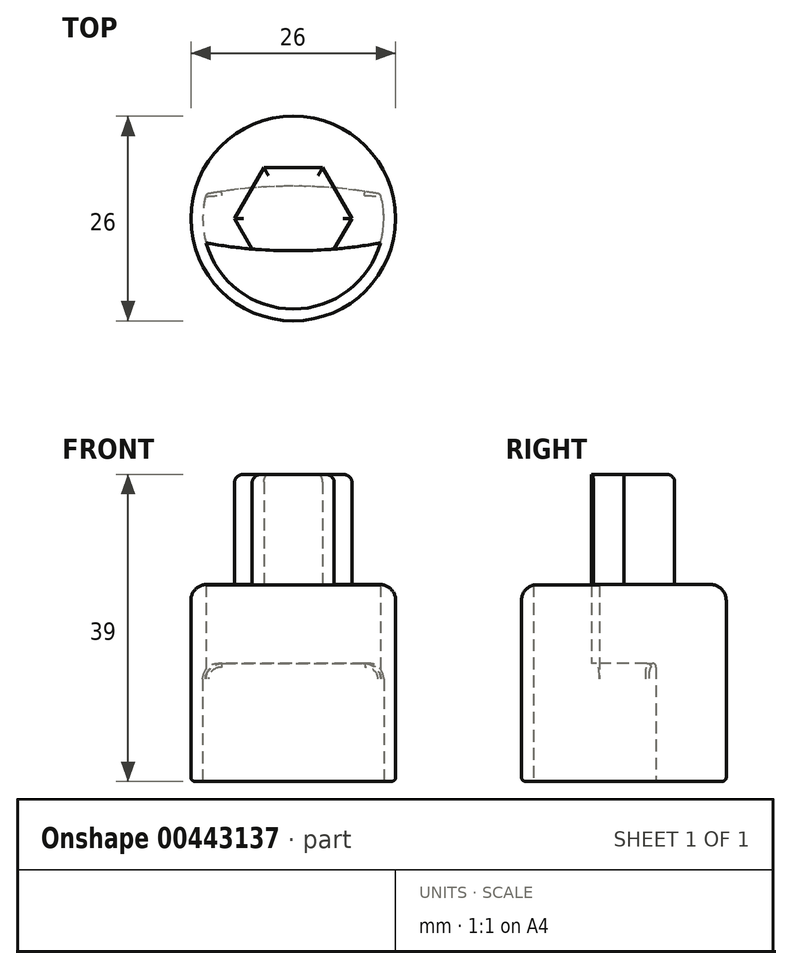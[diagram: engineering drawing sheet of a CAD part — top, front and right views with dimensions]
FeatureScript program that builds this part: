
annotation { "Feature Type Name" : "Feature", "Feature Type Description" : "" }
export const myFeature = defineFeature(function(context is Context, id is Id, definition is map)
    precondition{}
    {
        {
            var Q0;
            Q0=qCreatedBy(makeId("Top.planeOp"),FACE);
            var sketch = newSketch(context, id + "F0", { "sketchPlane" : qUnion([Q0])});
            skCircle(sketch, "E0", {"center": v(0, 0) * mm, "radius": 13 * mm});
            skCircle(sketch, "E1", {"center": v(0, 0) * mm, "radius": 11.5 * mm});
            skArc(sketch, "E2", {"start": v(11.07, 3.1) * mm, "mid": v(0, 4.1) * mm, "end": v(-11.07, 3.1) * mm});
            skLineSegment(sketch, "E3", {"start": v(-11.07, 3.1) * mm, "end": v(11.07, 3.1) * mm, "construction": true});
            skArc(sketch, "E4.MirrorCS", {"start": v(11.07, -3.1) * mm, "mid": v(0, -4.1) * mm, "end": v(-11.07, -3.1) * mm});
            skSolve(sketch);
        }
        {
            var Q0;
            Q0=makeQuery(id+"F0.imprint","IMPRINT",FACE,{"disambiguationData":[TD([[makeQuery(id+"F0.imprint","IMPRINT",EDGE,{"derivedFrom":sQuery(id+"F0.wireOp",EDGE,"E0")}),1.0]])]});
            var Q1;
            {var subQ0=sQuery(id+"F0.wireOp",EDGE,"E2");Q1=makeQuery(id+"F0.imprint","IMPRINT",FACE,{"disambiguationData":[TD([[makeQuery(id+"F0.imprint","IMPRINT",EDGE,{"derivedFrom":subQ0}),-1.0]])]});}
            var Q2;
            {var subQ0=sQuery(id+"F0.wireOp",EDGE,"E4.MirrorCS");Q2=makeQuery(id+"F0.imprint","IMPRINT",FACE,{"disambiguationData":[TD([[makeQuery(id+"F0.imprint","IMPRINT",EDGE,{"derivedFrom":subQ0}),1.0]])]});}
            var Q3;
            {var subQ0=sQuery(id+"F0.wireOp",EDGE,"E2");Q3=makeQuery(id+"F0.imprint","IMPRINT",FACE,{"disambiguationData":[TD([[makeQuery(id+"F0.imprint","IMPRINT",EDGE,{"derivedFrom":subQ0}),1.0]])]});}
            extrude(context, id + "F1", {"entities" : qUnion([Q0, Q1, Q2, Q3]), "depth" : 25 * mm});
        }
        {
            var Q0;
            {var subQ0=sQuery(id+"F0.wireOp",EDGE,"E2");Q0=makeQuery(id+"F0.imprint","IMPRINT",FACE,{"disambiguationData":[TD([[makeQuery(id+"F0.imprint","IMPRINT",EDGE,{"derivedFrom":subQ0}),1.0]])]});}
            extrude(context, id + "F2", {"entities" : qUnion([Q0]), "operationType" : NewBodyOperationType.REMOVE, "depth" : 15 * mm});
        }
        {
            var Q0;
            Q0=makeQuery(id+"F1.opExtrude","CAP_FACE",FACE,{"disambiguationData":[OSD([sQuery(id+"F0.wireOp",EDGE,"E0")])],"isStart":false});
            var sketch = newSketch(context, id + "F3", { "sketchPlane" : qUnion([Q0])});
            skCircle(sketch, "E5.cCircle", {"center": v(0, 0) * mm, "radius": 6.45 * mm, "construction": true});
            skLineSegment(sketch, "E5.0", {"start": v(-3.72, 6.45) * mm, "end": v(3.72, 6.45) * mm});
            skLineSegment(sketch, "E5.1", {"start": v(3.72, 6.45) * mm, "end": v(7.45, 0) * mm});
            skLineSegment(sketch, "E5.2", {"start": v(7.45, 0) * mm, "end": v(3.72, -6.45) * mm});
            skLineSegment(sketch, "E5.3", {"start": v(3.72, -6.45) * mm, "end": v(-3.72, -6.45) * mm});
            skLineSegment(sketch, "E5.4", {"start": v(-3.72, -6.45) * mm, "end": v(-7.45, 0) * mm});
            skLineSegment(sketch, "E5.5", {"start": v(-7.45, 0) * mm, "end": v(-3.72, 6.45) * mm});
            skPoint(sketch, "E5.0.midPoint", {"position": v(0, 6.45) * mm});
            skSolve(sketch);
        }
        {
            var Q0;
            Q0=makeQuery(id+"F3.imprint","IMPRINT",FACE,{"disambiguationData":[TD([[makeQuery(id+"F3.imprint","IMPRINT",EDGE,{"derivedFrom":sQuery(id+"F3.wireOp",EDGE,"E5.0")}),-1.0]])]});
            extrude(context, id + "F4", {"entities" : qUnion([Q0]), "operationType" : NewBodyOperationType.ADD, "depth" : 14 * mm});
        }
        {
            var Q0;
            Q0=makeQuery(id+"F4.opExtrude","CAP_EDGE",EDGE,{"disambiguationData":[OSD([sQuery(id+"F3.wireOp",EDGE,"E5.5")])],"isStart":true});
            var Q1;
            Q1=makeQuery(id+"F4.opExtrude","CAP_EDGE",EDGE,{"disambiguationData":[OSD([sQuery(id+"F3.wireOp",EDGE,"E5.4")])],"isStart":true});
            var Q2;
            Q2=makeQuery(id+"F4.opExtrude","CAP_EDGE",EDGE,{"disambiguationData":[OSD([sQuery(id+"F3.wireOp",EDGE,"E5.3")])],"isStart":true});
            var Q3;
            Q3=makeQuery(id+"F4.opExtrude","CAP_EDGE",EDGE,{"disambiguationData":[OSD([sQuery(id+"F3.wireOp",EDGE,"E5.2")])],"isStart":true});
            var Q4;
            Q4=makeQuery(id+"F4.opExtrude","CAP_EDGE",EDGE,{"disambiguationData":[OSD([sQuery(id+"F3.wireOp",EDGE,"E5.1")])],"isStart":true});
            var Q5;
            Q5=makeQuery(id+"F4.opExtrude","CAP_EDGE",EDGE,{"disambiguationData":[OSD([sQuery(id+"F3.wireOp",EDGE,"E5.0")])],"isStart":true});
            var Q6;
            Q6=makeQuery(id+"F4.opExtrude","CAP_EDGE",EDGE,{"disambiguationData":[OSD([sQuery(id+"F3.wireOp",EDGE,"E5.5")])],"isStart":false});
            var Q7;
            Q7=makeQuery(id+"F4.opExtrude","CAP_EDGE",EDGE,{"disambiguationData":[OSD([sQuery(id+"F3.wireOp",EDGE,"E5.0")])],"isStart":false});
            var Q8;
            Q8=makeQuery(id+"F4.opExtrude","CAP_EDGE",EDGE,{"disambiguationData":[OSD([sQuery(id+"F3.wireOp",EDGE,"E5.1")])],"isStart":false});
            var Q9;
            Q9=makeQuery(id+"F4.opExtrude","CAP_EDGE",EDGE,{"disambiguationData":[OSD([sQuery(id+"F3.wireOp",EDGE,"E5.4")])],"isStart":false});
            var Q10;
            Q10=makeQuery(id+"F4.opExtrude","CAP_EDGE",EDGE,{"disambiguationData":[OSD([sQuery(id+"F3.wireOp",EDGE,"E5.3")])],"isStart":false});
            var Q11;
            Q11=makeQuery(id+"F4.opExtrude","CAP_EDGE",EDGE,{"disambiguationData":[OSD([sQuery(id+"F3.wireOp",EDGE,"E5.2")])],"isStart":false});
            fillet(context, id + "F5", {"entities" : qUnion([Q0, Q1, Q2, Q3, Q4, Q5, Q6, Q7, Q8, Q9, Q10, Q11]), "radius" : 1 * mm, "tangentPropagation" : true, "allowEdgeOverflow" : false});
        }
        {
            var Q0;
            {var subQ0=sQuery(id+"F0.wireOp",EDGE,"E1");Q0=makeQuery(id+"F2.boolean.opBoolean","COPY",EDGE,{"derivedFrom":makeQuery(id+"F2.opExtrude","CAP_EDGE",EDGE,{"disambiguationData":[OSD([subQ0]),TDD([makeQuery(id+"F0.imprint","IMPRINT",EDGE,{"disambiguationData":[TD([[makeQuery(id+"F0.imprint","INTERSECT",VERTEX,{"disambiguationData":[OD(0.0)],"derivedFrom":[subQ0,sQuery(id+"F0.wireOp",EDGE,"E2")]}),1.0]])],"derivedFrom":subQ0})])],"isStart":false})});}
            var Q1;
            {var subQ0=sQuery(id+"F0.wireOp",EDGE,"E1");Q1=makeQuery(id+"F2.boolean.opBoolean","COPY",EDGE,{"derivedFrom":makeQuery(id+"F2.opExtrude","CAP_EDGE",EDGE,{"disambiguationData":[OSD([subQ0]),TDD([makeQuery(id+"F0.imprint","IMPRINT",EDGE,{"disambiguationData":[TD([[makeQuery(id+"F0.imprint","INTERSECT",VERTEX,{"disambiguationData":[OD(1.0)],"derivedFrom":[subQ0,sQuery(id+"F0.wireOp",EDGE,"E2")]}),-1.0]])],"derivedFrom":subQ0})])],"isStart":false})});}
            fillet(context, id + "F6", {"entities" : qUnion([Q0, Q1]), "radius" : 2 * mm, "tangentPropagation" : true, "allowEdgeOverflow" : false});
        }
        {
            var Q0;
            {var subQ0=sQuery(id+"F0.wireOp",EDGE,"E4.MirrorCS");var subQ1=sQuery(id+"F0.wireOp",EDGE,"E1");Q0=makeQuery(id+"F2.boolean.opBoolean","COPY",EDGE,{"derivedFrom":makeQuery(id+"F2.opExtrude","SWEPT_EDGE",EDGE,{"disambiguationData":[OSD([subQ1,subQ0]),TDD([makeQuery(id+"F0.imprint","INTERSECT",VERTEX,{"disambiguationData":[OD(0.0)],"derivedFrom":[subQ1,subQ0]})])]})});}
            var Q1;
            {var subQ0=sQuery(id+"F0.wireOp",EDGE,"E2");var subQ1=sQuery(id+"F0.wireOp",EDGE,"E1");Q1=makeQuery(id+"F2.boolean.opBoolean","COPY",EDGE,{"derivedFrom":makeQuery(id+"F2.opExtrude","SWEPT_EDGE",EDGE,{"disambiguationData":[OSD([subQ1,subQ0]),TDD([makeQuery(id+"F0.imprint","INTERSECT",VERTEX,{"disambiguationData":[OD(1.0)],"derivedFrom":[subQ1,subQ0]})])]})});}
            fillet(context, id + "F7", {"entities" : qUnion([Q0, Q1]), "radius" : 0.5 * mm, "tangentPropagation" : true, "allowEdgeOverflow" : false});
        }
        {
            var Q0;
            Q0=makeQuery(id+"F2.boolean.opBoolean","COPY",EDGE,{"derivedFrom":makeQuery(id+"F2.opExtrude","CAP_EDGE",EDGE,{"disambiguationData":[OSD([sQuery(id+"F0.wireOp",EDGE,"E4.MirrorCS")])],"isStart":true})});
            var Q1;
            Q1=makeQuery(id+"F1.opExtrude","CAP_EDGE",EDGE,{"disambiguationData":[OSD([sQuery(id+"F0.wireOp",EDGE,"E0")])],"isStart":true});
            fillet(context, id + "F8", {"entities" : qUnion([Q0, Q1]), "radius" : 0.5 * mm, "tangentPropagation" : true, "allowEdgeOverflow" : false});
        }
        {
            var Q0;
            Q0=makeQuery(id+"F1.opExtrude","CAP_EDGE",EDGE,{"disambiguationData":[OSD([sQuery(id+"F0.wireOp",EDGE,"E0")])],"isStart":false});
            fillet(context, id + "F9", {"entities" : qUnion([Q0]), "radius" : 2 * mm, "tangentPropagation" : true, "allowEdgeOverflow" : false});
        }
    });
